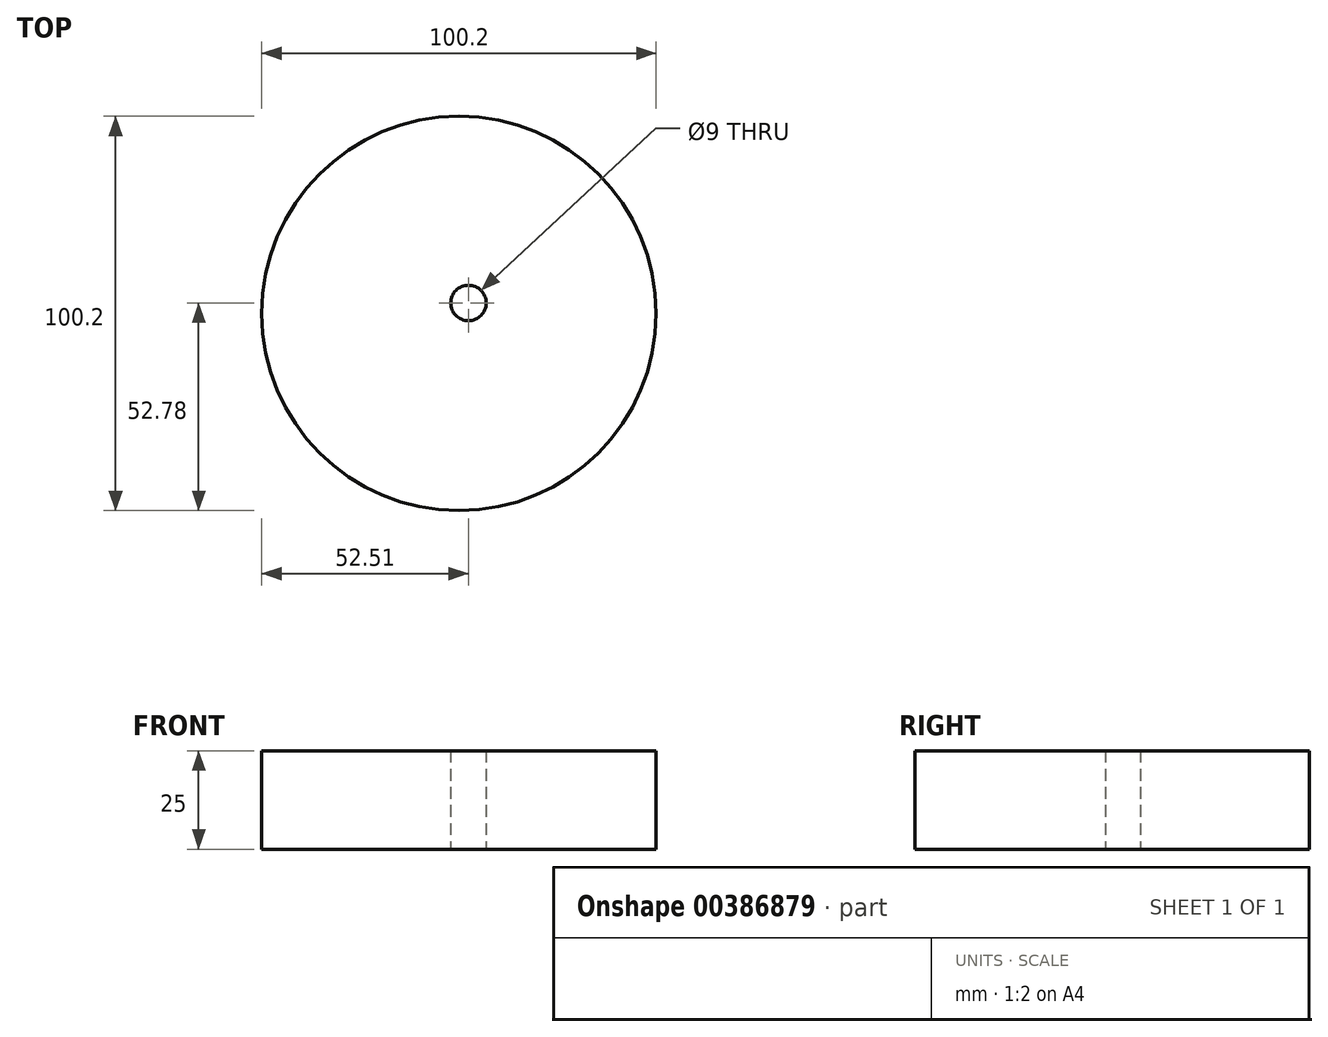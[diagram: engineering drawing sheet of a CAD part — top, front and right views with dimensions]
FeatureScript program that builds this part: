
annotation { "Feature Type Name" : "Feature", "Feature Type Description" : "" }
export const myFeature = defineFeature(function(context is Context, id is Id, definition is map)
    precondition{}
    {
        {
            var Q0;
            Q0=qCreatedBy(makeId("Top.planeOp"),FACE);
            var sketch = newSketch(context, id + "F0", { "sketchPlane" : qUnion([Q0])});
            skCircle(sketch, "E0", {"center": v(0, -2.68) * mm, "radius": 50.1 * mm});
            skCircle(sketch, "E1", {"center": v(2.4, 0) * mm, "radius": 4.5 * mm});
            skSolve(sketch);
        }
        {
            var Q0;
            Q0 = qSketchRegion(id + "F0", true);
            extrude(context, id + "F1", {"entities" : qUnion([Q0]), "depth" : 25 * mm});
        }
    });
